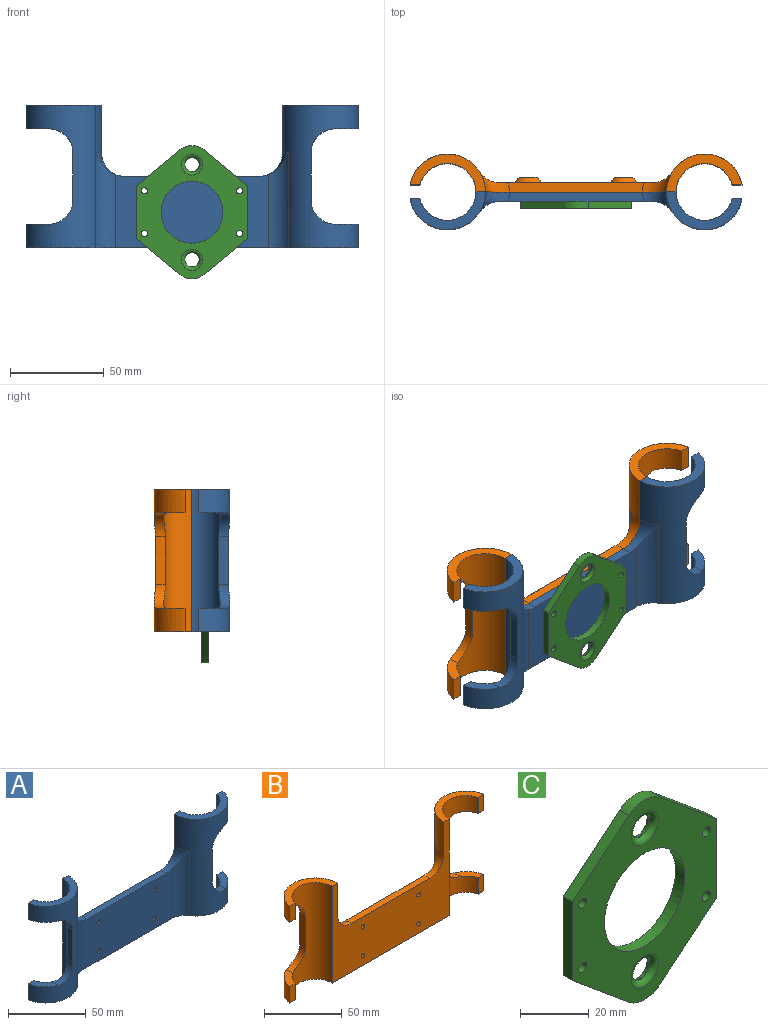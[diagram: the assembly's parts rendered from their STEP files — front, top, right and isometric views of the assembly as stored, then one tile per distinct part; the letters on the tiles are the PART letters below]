
ASSEMBLY  parts=3 mates=6
PART A: 33 faces, bbox 177.5x25.9x76.6 mm
  f0: plane 25.4x5.31mm, normal (-1,0,0), area 134.8mm2, adj f4,f5,f13,f14
  f1: plane 25.4x5.31mm, normal (1,0,0), area 134.8mm2, adj f6,f7,f19,f20
  f2: cylinder r=12.7mm len=50.8mm, axis (0,0,-1), area 571.6mm2, adj f15,f20,f22,f26
  f3: cylinder r=12.7mm len=50.8mm, axis (0,0,-1), area 571.6mm2, adj f10,f14,f22,f26
  f4: cylinder r=12.7mm len=12.7mm, axis (0,1,0), area 109.2mm2, adj f0,f8,f13,f14
  f5: cylinder r=12.7mm len=12.7mm, axis (0,1,0), area 109.2mm2, adj f0,f9,f13,f14
  f6: cylinder r=12.7mm len=12.7mm, axis (0,1,0), area 109.2mm2, adj f1,f16,f19,f20
  f7: cylinder r=12.7mm len=12.7mm, axis (0,1,0), area 109.2mm2, adj f1,f17,f19,f20
  f8: plane 15.03x12.34mm, normal (0,0,-1), area 82.3mm2, adj f4,f13,f14,f32
  f9: plane 15.03x12.34mm, normal (0,0,1), area 82.3mm2, adj f5,f13,f14,f31
  f10: bspline ~19.14x16.17mm, area 147.6mm2, adj f3,f12,f21,f26,f28
  f11: plane 40.28x20.2mm, normal (0,0,1), area 263.6mm2, adj f12,f13,f14,f28,f32
  f12: extruded ~25.4x10.81mm, area 290.3mm2, adj f10,f11,f14,f28
  f13: cylinder r=15.24mm len=76.2mm, axis (0,0,-1), area 2228.7mm2, adj f0,f4,f5,f8,f9,f11,f22,f28
  f14: cylinder r=20.32mm len=76.2mm, axis (0,0,-1), area 2168.7mm2, adj f0,f3,f4,f5,f8,f9,f11,f12
  f15: torus R=33.02mm, axis (0,0,1), area 149.1mm2, adj f2,f20,f21,f26,f28
  f16: plane 15.03x12.34mm, normal (0,0,1), area 82.3mm2, adj f6,f19,f20,f30
  f17: plane 15.03x12.34mm, normal (0,0,-1), area 82.3mm2, adj f7,f19,f20,f29
  f18: plane 40.28x20.19mm, normal (0,0,1), area 263.6mm2, adj f19,f20,f28,f29
  f19: cylinder r=15.24mm len=76.2mm, axis (0,0,-1), area 2228.7mm2, adj f1,f6,f7,f16,f17,f18,f22,f28
  f20: cylinder r=20.32mm len=76.2mm, axis (0,0,-1), area 2459mm2, adj f1,f2,f6,f7,f15,f16,f17,f18
  f21: plane 71.91x4.96mm, normal (0,0,1), area 353.6mm2, adj f10,f15,f26,f28
  f22: plane 177.08x20.19mm, normal (0,0,-1), area 1027.3mm2, adj f2,f3,f13,f14,f19,f20,f26,f28
  f23: cylinder r=1.65mm len=4.95mm, axis (0,-1,0), area 51.3mm2, adj f26,f28
  f24: cylinder r=1.65mm len=4.95mm, axis (0,-1,0), area 51.3mm2, adj f26,f28
  f25: cylinder r=1.65mm len=4.95mm, axis (0,-1,0), area 51.3mm2, adj f26,f28
  f26: plane 81.67x39.17mm, normal (0,-1,0), area 3074.3mm2, adj f2,f3,f10,f15,f21,f22,f23,f24
  f27: cylinder r=1.65mm len=4.95mm, axis (0,-1,0), area 51.3mm2, adj f26,f28
  f28: plane 107.12x76.63mm, normal (0,1,0), area 4486.7mm2, adj f10,f11,f12,f13,f15,f18,f19,f20
  f29: plane 12.7x5.2mm, normal (0,1,0), area 66.1mm2, adj f17,f18,f19,f20
  f30: plane 12.7x5.2mm, normal (0,1,0), area 66.1mm2, adj f16,f19,f20,f22
  f31: plane 12.7x5.2mm, normal (0,1,0), area 66.1mm2, adj f9,f13,f14,f22
  f32: plane 12.7x5.2mm, normal (0,1,0), area 66.1mm2, adj f8,f11,f13,f14
PART B: 69 faces, bbox 177.5x25.7x76.6 mm
  f0: plane 177.08x20.19mm, normal (0,0,-1), area 1027.3mm2, adj f6,f7,f8,f9,f10,f11,f12,f64
  f1: plane 6.93x6mm, normal (0,1,0), area 22.6mm2, adj f31,f53,f54,f55,f56,f57,f58
  f2: plane 6.93x6mm, normal (0,1,0), area 22.6mm2, adj f28,f46,f47,f48,f49,f50,f51
  f3: plane 6.93x6mm, normal (0,1,0), area 22.6mm2, adj f29,f39,f40,f41,f42,f43,f44
  f4: plane 6.93x6mm, normal (0,1,0), area 22.6mm2, adj f30,f32,f33,f34,f35,f36,f37
  f5: plane 71.91x4.96mm, normal (0,0,1), area 353.6mm2, adj f7,f16,f17,f64
  f6: cylinder r=12.7mm len=50.8mm, axis (0,0,-1), area 571.6mm2, adj f0,f7,f11,f16
  f7: plane 81.67x39.17mm, normal (0,1,0), area 2378.8mm2, adj f0,f5,f6,f8,f16,f17,f60,f61
  f8: cylinder r=12.7mm len=50.8mm, axis (0,0,-1), area 571.6mm2, adj f0,f7,f9,f17
  f9: cylinder r=20.32mm len=76.2mm, axis (0,0,-1), area 2168.7mm2, adj f0,f8,f13,f14,f18,f19,f20,f21
  f10: cylinder r=15.24mm len=76.2mm, axis (0,0,-1), area 2228.7mm2, adj f0,f14,f18,f19,f20,f21,f22,f64
  f11: cylinder r=20.32mm len=76.2mm, axis (0,0,-1), area 2459mm2, adj f0,f6,f15,f16,f23,f24,f25,f26
  f12: cylinder r=15.24mm len=76.2mm, axis (0,0,-1), area 2228.7mm2, adj f0,f15,f23,f24,f25,f26,f27,f64
  f13: extruded ~25.4x10.81mm, area 290.2mm2, adj f9,f14,f17,f64
  f14: plane 40.28x20.2mm, normal (0,0,1), area 263.6mm2, adj f9,f10,f13,f64,f68
  f15: plane 40.28x20.19mm, normal (0,0,1), area 263.6mm2, adj f11,f12,f64,f65
  f16: torus R=33.02mm, axis (0,0,1), area 149.1mm2, adj f5,f6,f7,f11,f64
  f17: bspline ~23.21x18.91mm, area 147.6mm2, adj f5,f7,f8,f13,f64
  f18: plane 15.03x12.34mm, normal (0,0,-1), area 82.3mm2, adj f9,f10,f19,f68
  f19: cylinder r=12.7mm len=12.7mm, axis (0,1,0), area 109.2mm2, adj f9,f10,f18,f20
  f20: plane 25.4x5.31mm, normal (-1,0,0), area 134.8mm2, adj f9,f10,f19,f21
  f21: cylinder r=12.7mm len=12.7mm, axis (0,1,0), area 109.2mm2, adj f9,f10,f20,f22
  f22: plane 15.03x12.34mm, normal (0,0,1), area 82.3mm2, adj f9,f10,f21,f67
  f23: plane 15.03x12.34mm, normal (0,0,1), area 82.3mm2, adj f11,f12,f24,f66
  f24: cylinder r=12.7mm len=12.7mm, axis (0,1,0), area 109.2mm2, adj f11,f12,f23,f25
  f25: plane 25.4x5.31mm, normal (1,0,0), area 134.8mm2, adj f11,f12,f24,f26
  f26: cylinder r=12.7mm len=12.7mm, axis (0,1,0), area 109.2mm2, adj f11,f12,f25,f27
  f27: plane 15.03x12.34mm, normal (0,0,-1), area 82.3mm2, adj f11,f12,f26,f65
  f28: cylinder r=1.65mm len=4.95mm, axis (0,-1,0), area 51.3mm2, adj f2,f64
  f29: cylinder r=1.65mm len=4.95mm, axis (0,-1,0), area 51.3mm2, adj f3,f64
  f30: cylinder r=1.65mm len=4.95mm, axis (0,-1,0), area 51.3mm2, adj f4,f64
  f31: cylinder r=1.65mm len=4.95mm, axis (0,-1,0), area 51.3mm2, adj f1,f64
  f32: plane 3x3mm, normal (-0.87,0,0.5), area 10.4mm2, adj f4,f33,f37,f38
  f33: plane 3x3mm, normal (-0.87,0,-0.5), area 10.4mm2, adj f4,f32,f34,f38
  f34: plane 3.46x3mm, normal (0,0,-1), area 10.4mm2, adj f4,f33,f35,f38
  f35: plane 3x3mm, normal (0.87,0,-0.5), area 10.4mm2, adj f4,f34,f36,f38
  f36: plane 3x3mm, normal (0.87,0,0.5), area 10.4mm2, adj f4,f35,f37,f38
  f37: plane 3.46x3mm, normal (0,0,1), area 10.4mm2, adj f4,f32,f36,f38
  f38: plane 9.24x9.24mm, normal (0,1,0), area 35.9mm2, adj f32,f33,f34,f35,f36,f37,f63
  f39: plane 3x3mm, normal (-0.87,0,-0.5), area 10.4mm2, adj f3,f40,f44,f45
  f40: plane 3.46x3mm, normal (0,0,-1), area 10.4mm2, adj f3,f39,f41,f45
  f41: plane 3x3mm, normal (0.87,0,-0.5), area 10.4mm2, adj f3,f40,f42,f45
  f42: plane 3x3mm, normal (0.87,0,0.5), area 10.4mm2, adj f3,f41,f43,f45
  f43: plane 3.46x3mm, normal (0,0,1), area 10.4mm2, adj f3,f42,f44,f45
  f44: plane 3x3mm, normal (-0.87,0,0.5), area 10.4mm2, adj f3,f39,f43,f45
  f45: plane 9.24x9.24mm, normal (0,1,0), area 35.9mm2, adj f39,f40,f41,f42,f43,f44,f62
  f46: plane 3x3mm, normal (-0.87,0,-0.5), area 10.4mm2, adj f2,f47,f51,f52
  f47: plane 3.46x3mm, normal (0,0,-1), area 10.4mm2, adj f2,f46,f48,f52
  f48: plane 3x3mm, normal (0.87,0,-0.5), area 10.4mm2, adj f2,f47,f49,f52
  f49: plane 3x3mm, normal (0.87,0,0.5), area 10.4mm2, adj f2,f48,f50,f52
  f50: plane 3.46x3mm, normal (0,0,1), area 10.4mm2, adj f2,f49,f51,f52
  f51: plane 3x3mm, normal (-0.87,0,0.5), area 10.4mm2, adj f2,f46,f50,f52
  f52: plane 9.24x9.24mm, normal (0,1,0), area 35.9mm2, adj f46,f47,f48,f49,f50,f51,f61
  f53: plane 3.46x3mm, normal (0,0,1), area 10.4mm2, adj f1,f54,f58,f59
  f54: plane 3x3mm, normal (-0.87,0,0.5), area 10.4mm2, adj f1,f53,f55,f59
  f55: plane 3x3mm, normal (-0.87,0,-0.5), area 10.4mm2, adj f1,f54,f56,f59
  f56: plane 3.46x3mm, normal (0,0,-1), area 10.4mm2, adj f1,f55,f57,f59
  f57: plane 3x3mm, normal (0.87,0,-0.5), area 10.4mm2, adj f1,f56,f58,f59
  f58: plane 3x3mm, normal (0.87,0,0.5), area 10.4mm2, adj f1,f53,f57,f59
  f59: plane 9.24x9.24mm, normal (0,1,0), area 35.9mm2, adj f53,f54,f55,f56,f57,f58,f60
  f60: cone r=4.62mm half-angle=45deg, axis (0,-1,0), area 163.1mm2, adj f7,f59
  f61: cone r=4.62mm half-angle=45deg, axis (0,-1,0), area 163.1mm2, adj f7,f52
  f62: cone r=4.62mm half-angle=45deg, axis (0,-1,0), area 163.1mm2, adj f7,f45
  f63: cone r=4.62mm half-angle=45deg, axis (0,-1,0), area 163.1mm2, adj f7,f38
  f64: plane 107.12x76.63mm, normal (0,-1,0), area 4486.7mm2, adj f0,f5,f10,f11,f12,f13,f14,f15
  f65: plane 12.7x5.2mm, normal (0,-1,0), area 66.1mm2, adj f11,f12,f15,f27
  f66: plane 12.7x5.2mm, normal (0,-1,0), area 66.1mm2, adj f0,f11,f12,f23
  f67: plane 12.7x5.2mm, normal (0,-1,0), area 66.1mm2, adj f0,f9,f10,f22
  f68: plane 12.7x5.2mm, normal (0,-1,0), area 66.1mm2, adj f9,f10,f14,f18
PART C: 21 faces, bbox 59.2x3.8x71.1 mm
  f0: plane 23.09x19.24mm, normal (0.64,0,0.77), area 114.5mm2, adj f1,f13,f15,f16
  f1: cylinder r=10.16mm len=13.01mm, axis (0,1,0), area 53.8mm2, adj f0,f2,f15,f16
  f2: plane 23.09x19.24mm, normal (-0.64,0,0.77), area 114.5mm2, adj f1,f3,f15,f16
  f3: plane 27.94x3.81mm, normal (-1,0,0), area 106.5mm2, adj f2,f4,f15,f16
  f4: plane 23.09x19.24mm, normal (-0.64,0,-0.77), area 114.5mm2, adj f3,f5,f15,f16
  f5: cylinder r=10.16mm len=13.01mm, axis (0,1,0), area 53.8mm2, adj f4,f6,f15,f16
  f6: plane 23.09x19.24mm, normal (0.64,0,-0.77), area 114.5mm2, adj f5,f13,f15,f16
  f7: cylinder r=3.81mm len=7.62mm, axis (0,1,0), area 6.1mm2, adj f17,f19
  f8: cylinder r=3.81mm len=7.62mm, axis (0,1,0), area 6.1mm2, adj f18,f20
  f9: cylinder r=1.65mm len=3.81mm, axis (0,1,0), area 39.5mm2, adj f15,f16
  f10: cylinder r=1.65mm len=3.81mm, axis (0,1,0), area 39.5mm2, adj f15,f16
  f11: cylinder r=1.65mm len=3.81mm, axis (0,1,0), area 39.5mm2, adj f15,f16
  f12: cylinder r=1.65mm len=3.81mm, axis (0,1,0), area 39.5mm2, adj f15,f16
  f13: plane 27.94x3.81mm, normal (1,0,0), area 106.5mm2, adj f0,f6,f15,f16
  f14: cylinder r=16.51mm len=33.02mm, axis (0,1,0), area 395.2mm2, adj f15,f16
  f15: plane 71.12x59.18mm, normal (0,-1,0), area 1997.2mm2, adj f0,f1,f2,f3,f4,f5,f6,f9
  f16: plane 71.12x59.18mm, normal (0,1,0), area 1997.2mm2, adj f0,f1,f2,f3,f4,f5,f6,f9
  f17: torus R=5.59mm, axis (0,-1,0), area 78.2mm2, adj f7,f16
  f18: torus R=5.59mm, axis (0,-1,0), area 78.2mm2, adj f8,f16
  f19: torus R=5.59mm, axis (0,-1,0), area 78.2mm2, adj f7,f15
  f20: torus R=5.59mm, axis (0,-1,0), area 78.2mm2, adj f8,f15
PLACE A t=(-29.4,-11.5,-40.61)mm
PLACE B t=(-29.4,-11.75,-40.61)mm
PLACE C t=(-29.4,-16.58,-21.56)mm
MATE planar A.f11 <-> B.f14  axis (0,0,1) through (-80.86,-22.44,35.59)mm
MATE cylindrical C.f12 <-> B.f28  axis (0,-1,0) through (-4,-20.39,-32.99)mm
MATE planar A.f21 <-> B.f5  axis (0,0,1) through (-29.4,-16.58,-2.51)mm
MATE planar C.f16 <-> A.f26  axis (0,1,0) through (0.19,-16.58,-21.56)mm
MATE planar B.f30 <-> A.f28  axis (0,-1,0) through (-54.8,-11.62,-10.13)mm
MATE cylindrical C.f10 <-> A.f25  axis (0,-1,0) through (-54.8,-20.39,-10.13)mm
